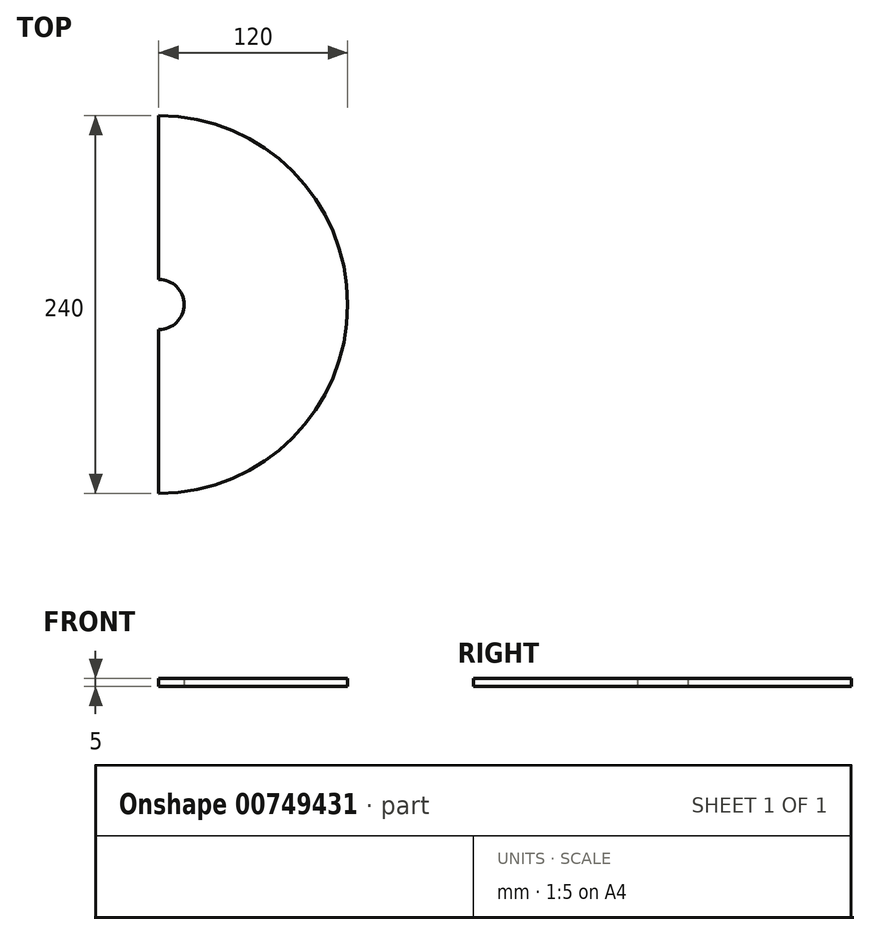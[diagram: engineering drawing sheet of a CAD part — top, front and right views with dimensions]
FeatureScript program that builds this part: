
annotation { "Feature Type Name" : "Feature", "Feature Type Description" : "" }
export const myFeature = defineFeature(function(context is Context, id is Id, definition is map)
    precondition{}
    {
        {
            var Q0;
            Q0=qCreatedBy(makeId("Top.planeOp"),FACE);
            var sketch = newSketch(context, id + "F0", { "sketchPlane" : qUnion([Q0])});
            skArc(sketch, "E0", {"start": v(0, -120) * mm, "mid": v(120, 0) * mm, "end": v(0, 120) * mm});
            skLineSegment(sketch, "E1", {"start": v(0, 120) * mm, "end": v(0, -120) * mm});
            skCircle(sketch, "E2", {"center": v(0, 0) * mm, "radius": 16 * mm});
            skLineSegment(sketch, "E3.left", {"start": v(0, 120) * mm, "end": v(0, 16) * mm});
            skLineSegment(sketch, "E4.left", {"start": v(0, -120) * mm, "end": v(0, -16) * mm});
            skPoint(sketch, "E3.top.end.orphan", {"position": v(-45, 16) * mm});
            skPoint(sketch, "E4.right.end.orphan", {"position": v(-45, -16) * mm});
            skSolve(sketch);
        }
        {
            var Q0;
            Q0=makeQuery(id+"F0.imprint","IMPRINT",FACE,{"disambiguationData":[TD([[makeQuery(id+"F0.imprint","IMPRINT",EDGE,{"derivedFrom":sQuery(id+"F0.wireOp",EDGE,"E3.bottom")}),1.0]])]});
            var Q1;
            Q1=makeQuery(id+"F0.imprint","IMPRINT",FACE,{"disambiguationData":[TD([[makeQuery(id+"F0.imprint","IMPRINT",EDGE,{"derivedFrom":sQuery(id+"F0.wireOp",EDGE,"E0")}),1.0]])]});
            var Q2;
            Q2=makeQuery(id+"F0.imprint","IMPRINT",FACE,{"disambiguationData":[TD([[makeQuery(id+"F0.imprint","IMPRINT",EDGE,{"derivedFrom":sQuery(id+"F0.wireOp",EDGE,"E4.bottom")}),-1.0]])]});
            extrude(context, id + "F1", {"entities" : qUnion([Q0, Q1, Q2]), "depth" : 5 * mm, "offsetDistance" : 25 * mm});
        }
    });
